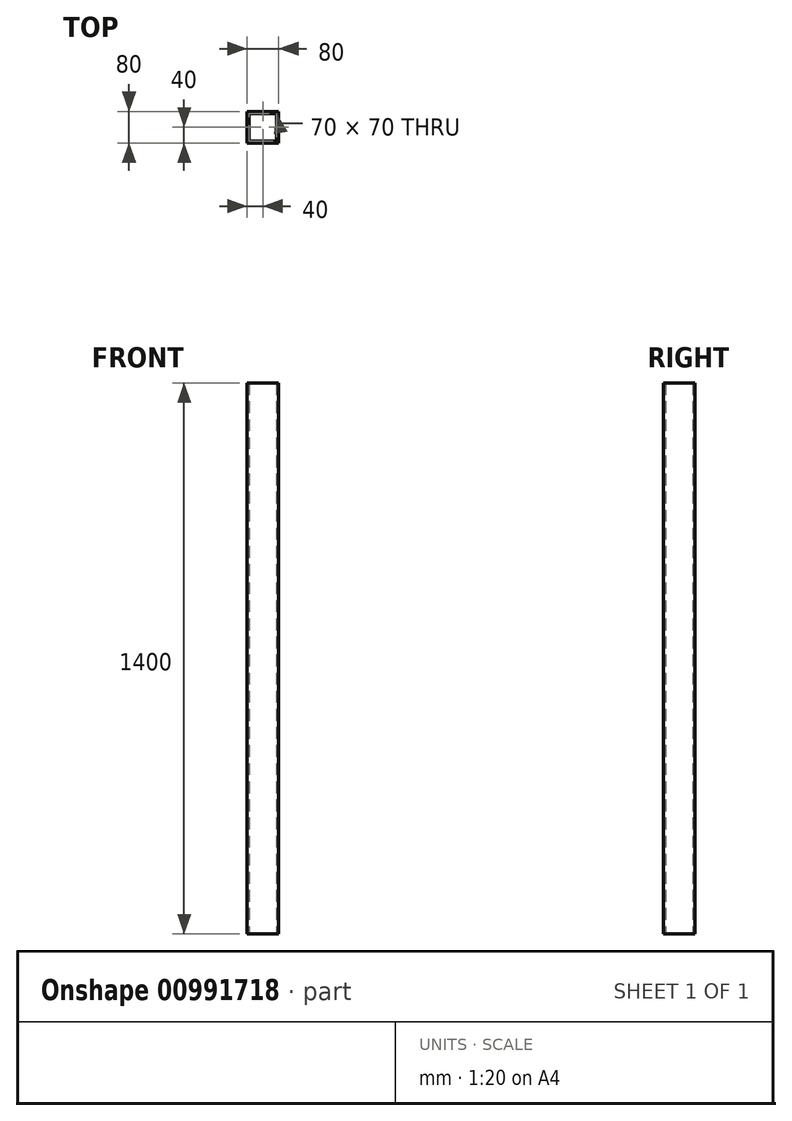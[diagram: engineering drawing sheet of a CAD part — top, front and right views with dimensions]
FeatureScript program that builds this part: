
annotation { "Feature Type Name" : "Feature", "Feature Type Description" : "" }
export const myFeature = defineFeature(function(context is Context, id is Id, definition is map)
    precondition{}
    {
        {
            var Q0;
            Q0=qCreatedBy(makeId("Top.planeOp"),FACE);
            var sketch = newSketch(context, id + "F0", { "sketchPlane" : qUnion([Q0])});
            skLineSegment(sketch, "E0.bottom", {"start": v(-40, 40) * mm, "end": v(40, 40) * mm});
            skLineSegment(sketch, "E0.top", {"start": v(-40, -40) * mm, "end": v(40, -40) * mm});
            skLineSegment(sketch, "E0.left", {"start": v(-40, 40) * mm, "end": v(-40, -40) * mm});
            skLineSegment(sketch, "E0.right", {"start": v(40, 40) * mm, "end": v(40, -40) * mm});
            skLineSegment(sketch, "E1.0", {"start": v(-35, 35) * mm, "end": v(35, 35) * mm});
            skLineSegment(sketch, "E1.1", {"start": v(-35, 35) * mm, "end": v(-35, -35) * mm});
            skLineSegment(sketch, "E1.2", {"start": v(-35, -35) * mm, "end": v(35, -35) * mm});
            skLineSegment(sketch, "E1.3", {"start": v(35, 35) * mm, "end": v(35, -35) * mm});
            skSolve(sketch);
        }
        {
            var Q0;
            Q0=makeQuery(id+"F0.imprint","IMPRINT",FACE,{"disambiguationData":[TD([[makeQuery(id+"F0.imprint","IMPRINT",EDGE,{"derivedFrom":sQuery(id+"F0.wireOp",EDGE,"E0.bottom")}),-1.0]])]});
            extrude(context, id + "F1", {"entities" : qUnion([Q0]), "depth" : 1400 * mm, "offsetDistance" : 25 * mm});
        }
    });
